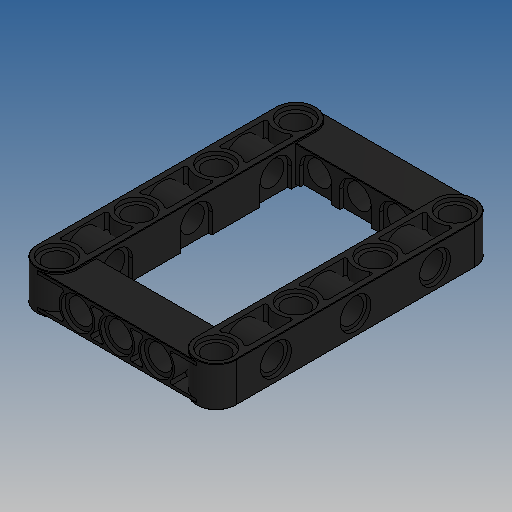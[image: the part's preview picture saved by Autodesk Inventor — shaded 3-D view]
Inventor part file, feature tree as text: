
AUTODESK INVENTOR PART (.ipt)
format: ipt  version: 2025 (Build 290162010, 162A)  size: 781,312 bytes
history: native  units: mm
features: extrude x13, sketch x9, mirror x3, fillet x2, projected_geometry x2, plane x1
ambient origin geometry x8: Origin, YZ Plane, XZ Plane, XY Plane, X Axis, Y Axis, Z Axis, Center Point
bodies: Solid1 (feature_tree)
feature tree (30):
  extrude  "Extrusion1"  Depth=0.8mm TaperAngle=0.0deg
  sketch  "Sketch6"  dims[d43=3.1mm d44=0.0mm d48=48.0mm]
  extrude  "Extrusion7"  Depth=3.1mm
  extrude  "Extrusion8"  Depth=4.8mm
  extrude  "Extrusion19"  Depth=0.4mm
  mirror  "Mirror5"
  sketch  "Sketch7"  dims[d49=6.4mm d50=4.8mm]
  extrude  "Extrusion9"  Depth=10.0mm
  extrude  "Extrusion10"  Depth=10.0mm TaperAngle=0.0deg
  extrude  "Extrusion11"  Depth=10.0mm
  extrude  "Extrusion18"  [1 undecoded]
  fillet  "Fillet2"  Radius=8.0mm
  plane  "Work Plane1"
  extrude  "Extrusion13"  Depth=5.8mm
  sketch  "Sketch12"  dims[d70=4.8mm d71=10.0mm d72=0.0mm]
  extrude  "Extrusion14"  Depth=3.1mm
  extrude  "Extrusion15"  Depth=3.1mm TaperAngle=0.0deg
  extrude  "Extrusion16"  Depth=3.1mm
  extrude  "Extrusion17"  Depth=3.1mm
  fillet  "Fillet3"  Radius=0.9mm
  mirror  "Mirror4"
  mirror  "Mirror3"
  projected_geometry  "Projected Loop4"
  sketch  "Skizze - Rechteckige Anordnung1"  dims[d14=8.0mm d15=0.0mm d41=0.8mm d42=0.0mm]
  sketch  "Sketch8"  dims[d51=16.0mm d60=0.4mm d61=0.1mm]
  sketch  "Sketch11"  dims[d62=30.0mm d64=16.0mm d65=10.0mm d67=10.0mm d69=7.2mm]
  projected_geometry  "Projected Loop5"
  sketch  "Sketch13"  dims[d73=10.0mm d74=0.0mm d75=6.2mm]
  sketch  "Sketch14"  dims[d76=0.8mm d77=0.0mm d78=-16.0mm d86=8.0mm]
  sketch  "Sketch15"  dims[d87=3.1mm d88=5.8mm d89=7.2mm d90=0.9mm d91=0.0mm d92=4.8mm d93=6.4mm d94=0.9mm d95=0.0mm d96=0.9mm d97=0.0mm d98=0.8mm d99=0.0mm d100=6.4mm d101=0.8mm d102=0.0mm d103=0.1mm d104=0.4mm d106=6.4mm d107=0.8mm d108=0.0mm d109=45.0deg d111=1.6mm d112=3.1mm d113=0.0mm d114=16.0mm d116=45.0deg d117=56.0mm d118=8.0mm]
note: 1 required parameter value undecoded (feature->parameter linkage not recoverable at this tier; creation-order binding heuristic only, values carry confidence <= 0.55)
